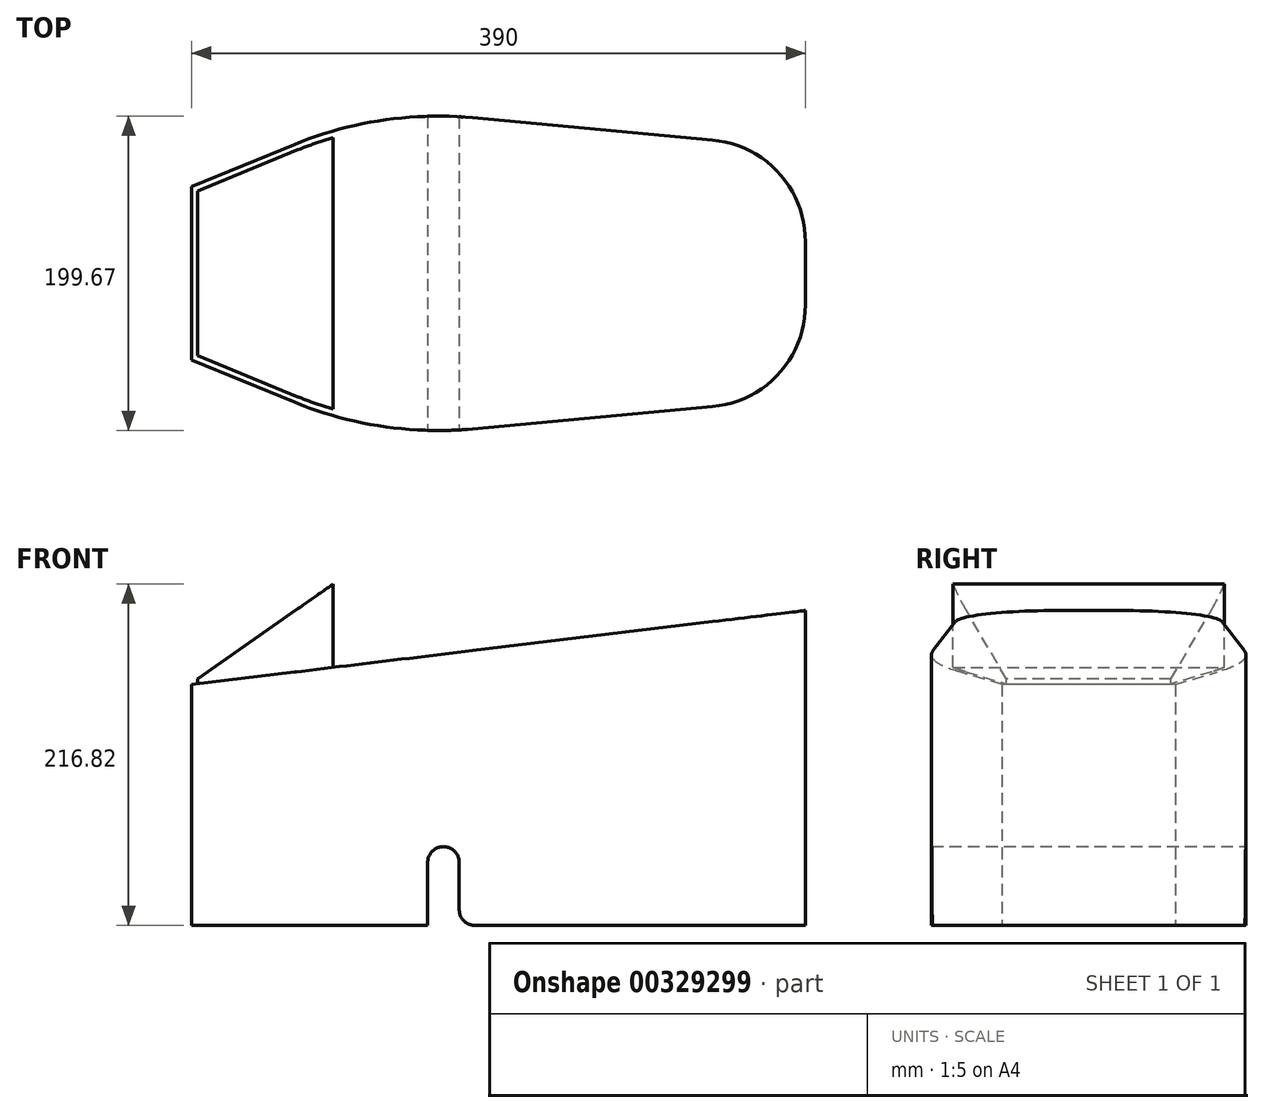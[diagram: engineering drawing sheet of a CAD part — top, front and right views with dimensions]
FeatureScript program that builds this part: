
annotation { "Feature Type Name" : "Feature", "Feature Type Description" : "" }
export const myFeature = defineFeature(function(context is Context, id is Id, definition is map)
    precondition{}
    {
        {
            var Q0;
            Q0=qCreatedBy(makeId("Top.planeOp"),FACE);
            var sketch = newSketch(context, id + "F0", { "sketchPlane" : qUnion([Q0])});
            skLineSegment(sketch, "E0", {"start": v(-195, 55.25) * mm, "end": v(-195, -54.75) * mm});
            skArc(sketch, "E1", {"start": v(135.99, -84.47) * mm, "mid": v(178.03, -63.54) * mm, "end": v(195, -19.75) * mm});
            skPoint(sketch, "E2.orphan", {"position": v(-195, -65.85) * mm});
            skLineSegment(sketch, "E3", {"start": v(-195, 0.25) * mm, "end": v(195, 0.25) * mm});
            skLineSegment(sketch, "E4", {"start": v(-16.4, -98.56) * mm, "end": v(135.99, -84.47) * mm});
            skLineSegment(sketch, "E5", {"start": v(-223.32, -54.75) * mm, "end": v(-188.1, -54.75) * mm, "construction": true});
            skLineSegment(sketch, "E6", {"start": v(-195, -54.75) * mm, "end": v(-129.7, -81.57) * mm});
            skArc(sketch, "E7.filletArc", {"start": v(-129.7, -81.57) * mm, "mid": v(-74.07, -96.93) * mm, "end": v(-16.4, -98.56) * mm});
            skLineSegment(sketch, "E8.trimOffspring", {"start": v(195, 20.25) * mm, "end": v(195, -19.75) * mm});
            skLineSegment(sketch, "E9.MirrorCS", {"start": v(-223.32, 55.25) * mm, "end": v(-188.1, 55.25) * mm, "construction": true});
            skPoint(sketch, "E10.MirrorP", {"position": v(-195, 66.36) * mm});
            skLineSegment(sketch, "E11.MirrorCS", {"start": v(-195, 55.25) * mm, "end": v(-129.7, 82.08) * mm});
            skLineSegment(sketch, "E12.MirrorCS", {"start": v(-16.4, 99.07) * mm, "end": v(135.99, 84.98) * mm});
            skArc(sketch, "E13.MirrorCS", {"start": v(-129.7, 82.08) * mm, "mid": v(-74.07, 97.44) * mm, "end": v(-16.4, 99.07) * mm});
            skArc(sketch, "E14.MirrorCS", {"start": v(135.99, 84.98) * mm, "mid": v(178.03, 64.05) * mm, "end": v(195, 20.25) * mm});
            skSolve(sketch);
        }
        {
            var Q0;
            Q0=makeQuery(id+"F0.imprint","IMPRINT",FACE,{"disambiguationData":[TD([[makeQuery(id+"F0.imprint","IMPRINT",EDGE,{"derivedFrom":sQuery(id+"F0.wireOp",EDGE,"E0")}),1.0]])]});
            extrude(context, id + "F1", {"entities" : qUnion([Q0]), "depth" : 200 * mm});
        }
        {
            var Q0;
            Q0=qCreatedBy(makeId("Top.planeOp"),FACE);
            cPlane(context, id + "F2", {"entities" : qUnion([Q0]), "cplaneType" : CPlaneType.OFFSET, "offset" : 220 * mm, "width" : 150 * mm, "height" : 150 * mm});
        }
        {
            var Q0;
            Q0=qCreatedBy(makeId("Front.planeOp"),FACE);
            var sketch = newSketch(context, id + "F3", { "sketchPlane" : qUnion([Q0])});
            skLineSegment(sketch, "E15.0", {"start": v(-195, 200) * mm, "end": v(-195, 153) * mm});
            skLineSegment(sketch, "E16", {"start": v(-195, 200) * mm, "end": v(195, 200) * mm});
            skLineSegment(sketch, "E17", {"start": v(195, 200) * mm, "end": v(-195, 153) * mm});
            skPoint(sketch, "E18.orphan", {"position": v(-195, 0) * mm});
            skPoint(sketch, "E19.0.end.orphan", {"position": v(195, 0) * mm});
            skSolve(sketch);
        }
        {
            var Q0;
            Q0 = qSketchRegion(id + "F3", true);
            extrude(context, id + "F4", {"entities" : qUnion([Q0]), "operationType" : NewBodyOperationType.REMOVE, "endBound" : BoundingType.SYMMETRIC, "oppositeDirection" : true, "depth" : 220 * mm});
        }
        {
            var Q0;
            Q0=qCreatedBy(makeId("Front.planeOp"),FACE);
            var sketch = newSketch(context, id + "F5", { "sketchPlane" : qUnion([Q0])});
            skLineSegment(sketch, "E20", {"start": v(-25, 50) * mm, "end": v(-25, 0) * mm});
            skLineSegment(sketch, "E21.0", {"start": v(195, 200) * mm, "end": v(195, 0) * mm, "construction": true});
            skLineSegment(sketch, "E22.0", {"start": v(-45, 50) * mm, "end": v(-45, 0) * mm});
            skLineSegment(sketch, "E23", {"start": v(-45, 50) * mm, "end": v(-25, 50) * mm});
            skPoint(sketch, "E24.orphan", {"position": v(-25, 136.96) * mm});
            skLineSegment(sketch, "E25.trimOffspring", {"start": v(195, 50) * mm, "end": v(252.37, 50) * mm, "construction": true});
            skPoint(sketch, "E26.orphan", {"position": v(-25, -19.1) * mm});
            skPoint(sketch, "E27.orphan", {"position": v(-16.4, 0) * mm});
            skLineSegment(sketch, "E28.trimOffspring", {"start": v(-45, 0) * mm, "end": v(-25, 0) * mm});
            skSolve(sketch);
        }
        {
            var Q0;
            Q0 = qSketchRegion(id + "F5", true);
            extrude(context, id + "F6", {"entities" : qUnion([Q0]), "operationType" : NewBodyOperationType.REMOVE, "endBound" : BoundingType.SYMMETRIC, "oppositeDirection" : true, "depth" : 220 * mm});
        }
        {
            var Q0;
            Q0=makeQuery(id+"F6.boolean.opBoolean","COPY",EDGE,{"derivedFrom":makeQuery(id+"F6.opExtrude","SWEPT_EDGE",EDGE,{"disambiguationData":[OSD([sQuery(id+"F5.wireOp",EDGE,"E20"),sQuery(id+"F5.wireOp",EDGE,"E23")])]})});
            var Q1;
            Q1=makeQuery(id+"F6.boolean.opBoolean","COPY",EDGE,{"derivedFrom":makeQuery(id+"F6.opExtrude","SWEPT_EDGE",EDGE,{"disambiguationData":[OSD([sQuery(id+"F5.wireOp",EDGE,"E22.0"),sQuery(id+"F5.wireOp",EDGE,"E23")])]})});
            fillet(context, id + "F7", {"entities" : qUnion([Q0, Q1]), "radius" : 10 * mm, "tangentPropagation" : true, "allowEdgeOverflow" : false});
        }
        {
            var Q0;
            Q0=makeQuery(id+"F6.boolean.opBoolean","COPY",EDGE,{"derivedFrom":makeQuery(id+"F6.opExtrude","SWEPT_EDGE",EDGE,{"disambiguationData":[OSD([sQuery(id+"F5.wireOp",EDGE,"E22.0"),sQuery(id+"F5.wireOp",EDGE,"E28.trimOffspring")])]})});
            var Q1;
            Q1=makeQuery(id+"F6.boolean.opBoolean","COPY",EDGE,{"derivedFrom":makeQuery(id+"F6.opExtrude","SWEPT_EDGE",EDGE,{"disambiguationData":[OSD([sQuery(id+"F5.wireOp",EDGE,"E20"),sQuery(id+"F5.wireOp",EDGE,"E28.trimOffspring")])]})});
            fillet(context, id + "F8", {"entities" : qUnion([Q0, Q1]), "radius" : 10 * mm, "tangentPropagation" : true, "allowEdgeOverflow" : false});
        }
        {
            var Q0;
            Q0=qCreatedBy(id+"F2.planeOp",FACE);
            var sketch = newSketch(context, id + "F9", { "sketchPlane" : qUnion([Q0])});
            skLineSegment(sketch, "E29.0", {"start": v(-195, 55.25) * mm, "end": v(-129.7, 82.08) * mm, "construction": true});
            skLineSegment(sketch, "E30.0", {"start": v(-195, 55.25) * mm, "end": v(-195, -54.75) * mm, "construction": true});
            skLineSegment(sketch, "E31.0", {"start": v(-195, -54.75) * mm, "end": v(-129.7, -81.57) * mm, "construction": true});
            skArc(sketch, "E32.0", {"start": v(-129.7, 82.08) * mm, "mid": v(-117.47, 86.72) * mm, "end": v(-105, 90.7) * mm, "construction": true});
            skArc(sketch, "E33.0", {"start": v(-129.7, -81.57) * mm, "mid": v(-117.47, -86.22) * mm, "end": v(-105, -90.18) * mm, "construction": true});
            skLineSegment(sketch, "E34", {"start": v(-105, 86.52) * mm, "end": v(-105, -86.02) * mm});
            skArc(sketch, "E35.0", {"start": v(-128.18, 78.38) * mm, "mid": v(-116.7, 82.76) * mm, "end": v(-105, 86.52) * mm});
            skArc(sketch, "E35.1", {"start": v(-128.18, -77.87) * mm, "mid": v(-116.7, -82.25) * mm, "end": v(-105, -86.02) * mm});
            skLineSegment(sketch, "E35.2", {"start": v(-191, -52.06) * mm, "end": v(-128.18, -77.87) * mm});
            skLineSegment(sketch, "E35.3", {"start": v(-191, 52.57) * mm, "end": v(-191, -52.06) * mm});
            skLineSegment(sketch, "E35.4", {"start": v(-191, 52.57) * mm, "end": v(-128.18, 78.38) * mm});
            skSolve(sketch);
        }
        {
            var Q0;
            Q0 = qSketchRegion(id + "F9", true);
            extrude(context, id + "F10", {"entities" : qUnion([Q0]), "operationType" : NewBodyOperationType.ADD, "endBound" : BoundingType.UP_TO_NEXT, "oppositeDirection" : true, "depth" : 25 * mm});
        }
        {
            var Q0;
            Q0=qCreatedBy(makeId("Front.planeOp"),FACE);
            var sketch = newSketch(context, id + "F11", { "sketchPlane" : qUnion([Q0])});
            skLineSegment(sketch, "E36.0", {"start": v(-128.18, 161.05) * mm, "end": v(-191, 153.48) * mm, "construction": true});
            skLineSegment(sketch, "E37.0", {"start": v(-105, 163.85) * mm, "end": v(-128.18, 161.05) * mm, "construction": true});
            skLineSegment(sketch, "E38.0", {"start": v(-128.54, 164.03) * mm, "end": v(-191, 156.5) * mm, "construction": true});
            skLineSegment(sketch, "E38.1", {"start": v(-105.36, 166.82) * mm, "end": v(-128.54, 164.03) * mm, "construction": true});
            skLineSegment(sketch, "E39.0", {"start": v(-105, 216.82) * mm, "end": v(-105, 220) * mm});
            skLineSegment(sketch, "E40", {"start": v(-191, 156.5) * mm, "end": v(-105, 216.82) * mm});
            skLineSegment(sketch, "E41.0", {"start": v(-191, 220) * mm, "end": v(-105, 220) * mm});
            skLineSegment(sketch, "E42.0", {"start": v(-191, 153.48) * mm, "end": v(-191, 220) * mm});
            skPoint(sketch, "E43.orphan", {"position": v(-128.18, 220) * mm});
            skSolve(sketch);
        }
        {
            var Q0;
            Q0 = qSketchRegion(id + "F11", true);
            extrude(context, id + "F12", {"entities" : qUnion([Q0]), "operationType" : NewBodyOperationType.REMOVE, "endBound" : BoundingType.SYMMETRIC, "oppositeDirection" : true, "depth" : 200 * mm});
        }
    });
